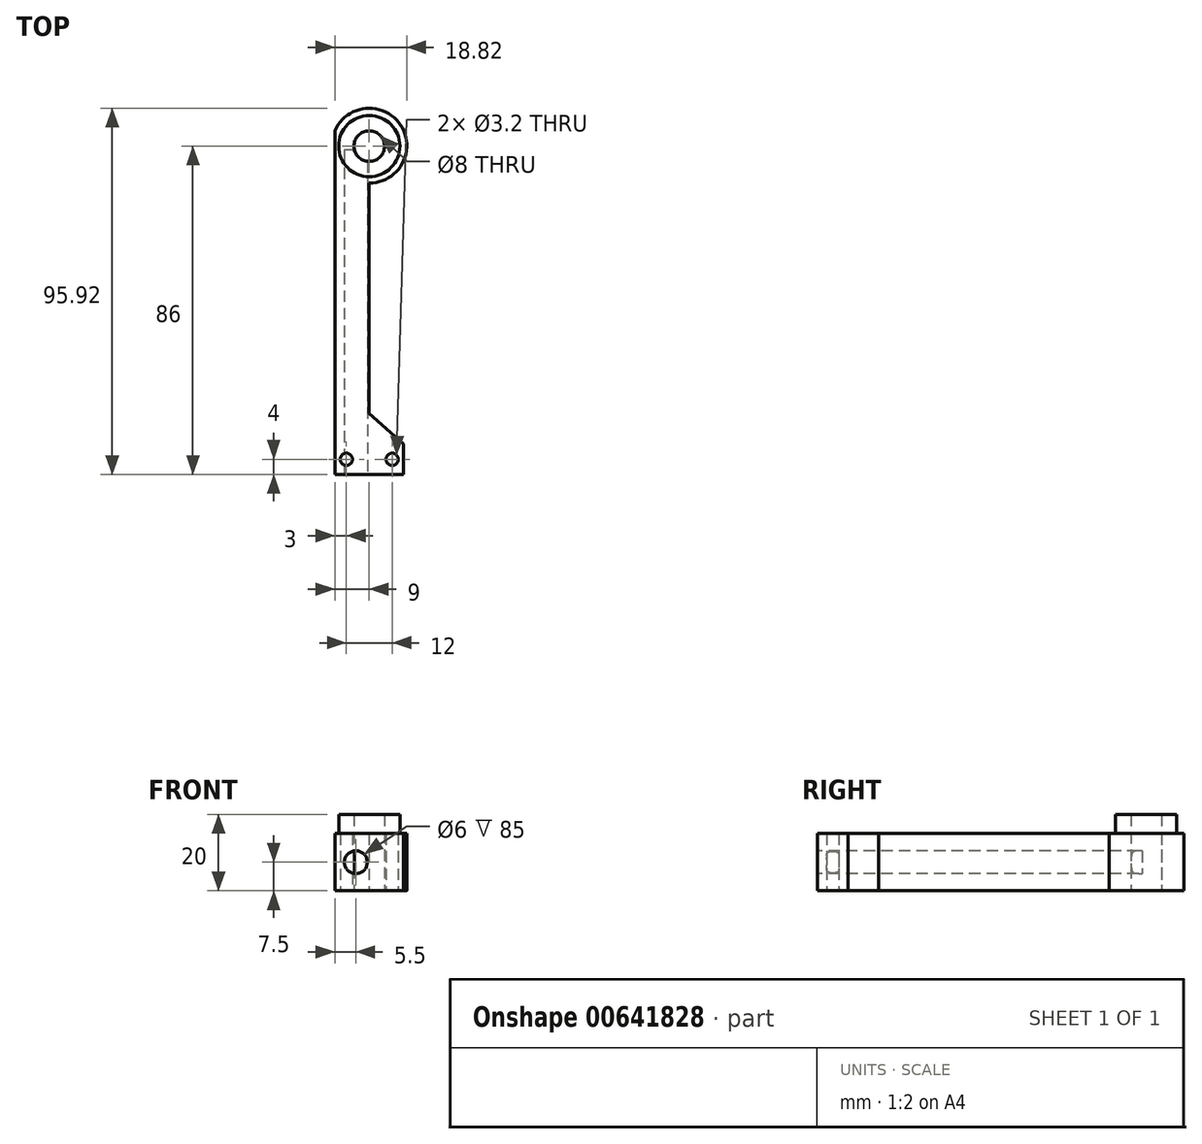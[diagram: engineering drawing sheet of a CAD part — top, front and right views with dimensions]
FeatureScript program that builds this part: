
annotation { "Feature Type Name" : "Feature", "Feature Type Description" : "" }
export const myFeature = defineFeature(function(context is Context, id is Id, definition is map)
    precondition{}
    {
        {
            var Q0;
            Q0=qCreatedBy(makeId("Top.planeOp"),FACE);
            var sketch = newSketch(context, id + "F0", { "sketchPlane" : qUnion([Q0])});
            skLineSegment(sketch, "E0", {"start": v(0, 90) * mm, "end": v(0, 0) * mm});
            skLineSegment(sketch, "E1", {"start": v(0, 0) * mm, "end": v(18, 0) * mm});
            skLineSegment(sketch, "E2", {"start": v(18, 0) * mm, "end": v(18, 8) * mm});
            skLineSegment(sketch, "E3", {"start": v(18, 8) * mm, "end": v(9, 16) * mm});
            skLineSegment(sketch, "E4", {"start": v(9, 16) * mm, "end": v(9, 46) * mm});
            skLineSegment(sketch, "E5", {"start": v(9, 46) * mm, "end": v(9, 86) * mm});
            skLineSegment(sketch, "E6", {"start": v(15, 4) * mm, "end": v(3, 4) * mm});
            skPoint(sketch, "E6.startSnap0", {"position": v(19, 4) * mm});
            skCircle(sketch, "E7", {"center": v(3, 4) * mm, "radius": 1.6 * mm});
            skCircle(sketch, "E8", {"center": v(15, 4) * mm, "radius": 1.6 * mm});
            skCircle(sketch, "E9", {"center": v(9, 86) * mm, "radius": 4 * mm});
            skCircle(sketch, "E10", {"center": v(9, 86) * mm, "radius": 8 * mm});
            skLineSegment(sketch, "E11", {"start": v(9, 86) * mm, "end": v(11.83, 83.17) * mm});
            skLineSegment(sketch, "E12", {"start": v(3.34, 80.34) * mm, "end": v(9, 86) * mm});
            skLineSegment(sketch, "E13", {"start": v(6.17, 88.83) * mm, "end": v(9, 86) * mm});
            skArc(sketch, "E14", {"start": v(9, 76.3) * mm, "mid": v(17.2, 91.5) * mm, "end": v(0, 90) * mm});
            skCircle(sketch, "E15", {"center": v(9, 86.11) * mm, "radius": 2 * mm});
            skSolve(sketch);
        }
        {
            var Q0;
            {var subQ3=sQuery(id+"F0.wireOp",EDGE,"E5");var subQ7=sQuery(id+"F0.wireOp",EDGE,"E10");var subQ8=makeQuery(id+"F0.imprint","INTERSECT",VERTEX,{"derivedFrom":[subQ3,subQ7]});Q0=makeQuery(id+"F0.imprint","IMPRINT",FACE,{"disambiguationData":[TD([[makeQuery(id+"F0.imprint","IMPRINT",EDGE,{"disambiguationData":[TD([[subQ8,-1.0]])],"derivedFrom":subQ3}),-1.0]])]});}
            var Q1;
            {var subQ0=sQuery(id+"F0.wireOp",EDGE,"E10");var subQ1=sQuery(id+"F0.wireOp",EDGE,"E5");var subQ2=makeQuery(id+"F0.imprint","INTERSECT",VERTEX,{"derivedFrom":[subQ1,subQ0]});Q1=makeQuery(id+"F0.imprint","IMPRINT",FACE,{"disambiguationData":[TD([[makeQuery(id+"F0.imprint","IMPRINT",EDGE,{"disambiguationData":[TD([[subQ2,-1.0]])],"derivedFrom":subQ1}),1.0]])]});}
            extrude(context, id + "F1", {"entities" : qUnion([Q0, Q1]), "depth" : 20 * mm, "offsetDistance" : 25 * mm});
        }
        {
            var Q0;
            Q0=makeQuery(id+"F0.imprint","IMPRINT",FACE,{"disambiguationData":[TD([[makeQuery(id+"F0.imprint","IMPRINT",EDGE,{"derivedFrom":sQuery(id+"F0.wireOp",EDGE,"E0")}),1.0]])]});
            extrude(context, id + "F2", {"entities" : qUnion([Q0]), "operationType" : NewBodyOperationType.ADD, "depth" : 15 * mm, "offsetDistance" : 25 * mm});
        }
        {
            var Q0;
            Q0=makeQuery(id+"F2.opExtrude","SWEPT_FACE",FACE,{"disambiguationData":[OSD([sQuery(id+"F0.wireOp",EDGE,"E1")])]});
            var sketch = newSketch(context, id + "F3", { "sketchPlane" : qUnion([Q0])});
            skSolve(sketch);
        }
        {
            var Q0;
            {var subQ0=sQuery(id+"F0.wireOp",EDGE,"E1");Q0=makeQuery(id+"F3.imprint","IMPRINT",FACE,{"disambiguationData":[TD([[makeQuery(id+"F3.imprint","IMPRINT",EDGE,{"derivedFrom":makeQuery(id+"F2.opExtrude","CAP_EDGE",EDGE,{"disambiguationData":[OSD([subQ0])],"isStart":true})}),1.0]])]});}
            var sketch = newSketch(context, id + "F4", { "sketchPlane" : qUnion([Q0])});
            skCircle(sketch, "E16", {"center": v(5.5, 7.5) * mm, "radius": 3 * mm});
            skSolve(sketch);
        }
        {
            var Q0;
            Q0 = qSketchRegion(id + "F4", true);
            extrude(context, id + "F5", {"entities" : qUnion([Q0]), "operationType" : NewBodyOperationType.REMOVE, "oppositeDirection" : true, "depth" : 85 * mm, "offsetDistance" : 25 * mm});
        }
    });
